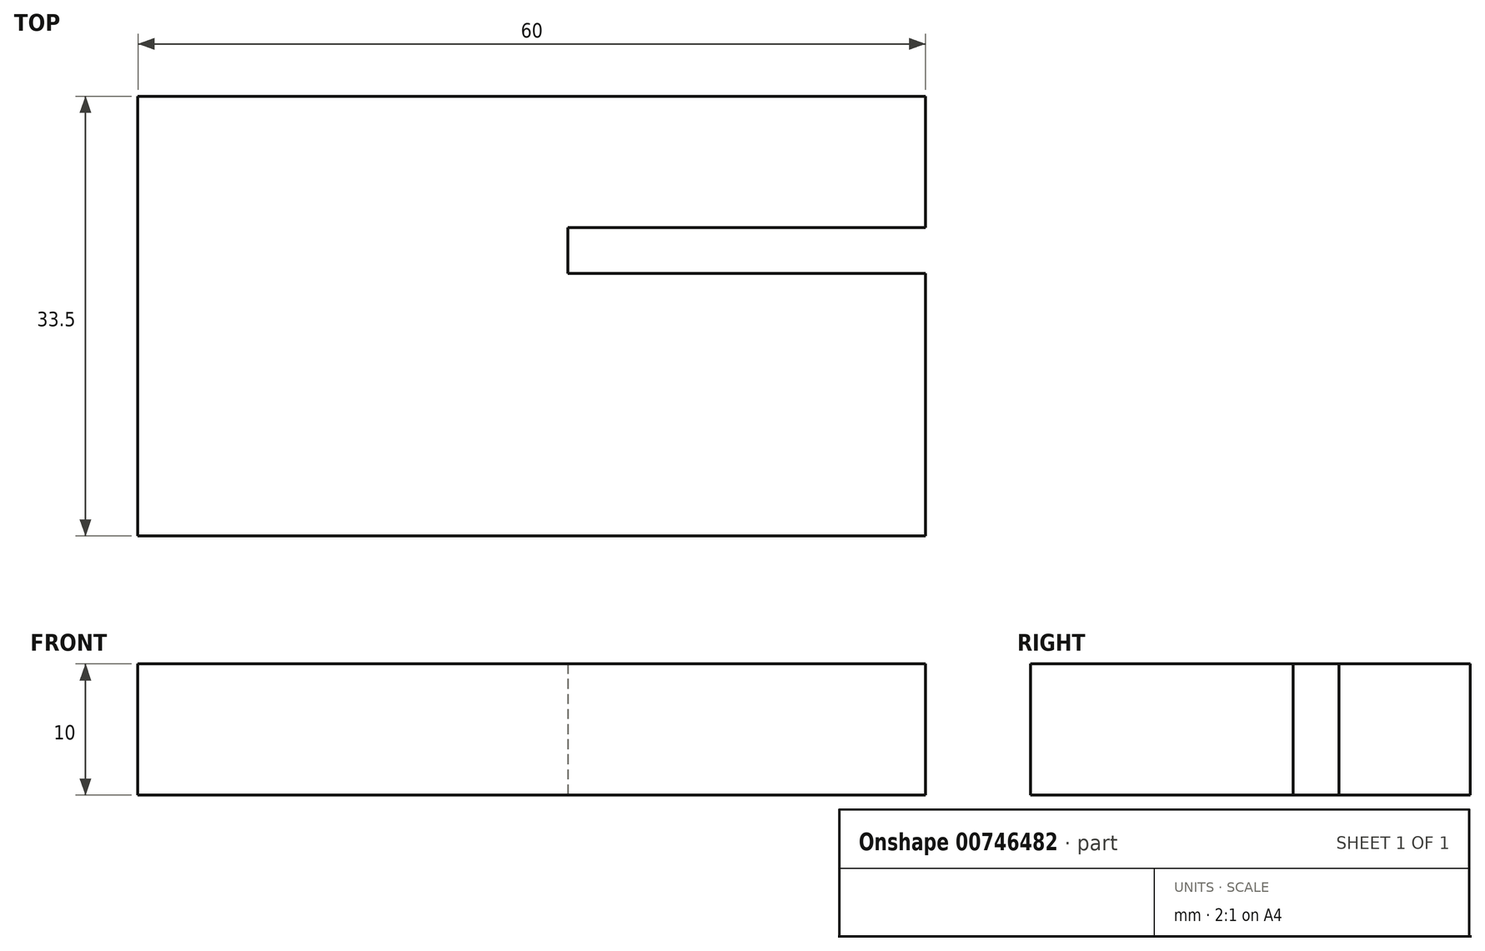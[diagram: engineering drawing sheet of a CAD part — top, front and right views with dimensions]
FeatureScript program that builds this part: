
annotation { "Feature Type Name" : "Feature", "Feature Type Description" : "" }
export const myFeature = defineFeature(function(context is Context, id is Id, definition is map)
    precondition{}
    {
        {
            var Q0;
            Q0=qCreatedBy(makeId("Top.planeOp"),FACE);
            var sketch = newSketch(context, id + "F0", { "sketchPlane" : qUnion([Q0])});
            skLineSegment(sketch, "E0", {"start": v(0, 0) * mm, "end": v(43.84, 0) * mm});
            skLineSegment(sketch, "E1", {"start": v(43.84, 0) * mm, "end": v(43.84, -10) * mm});
            skLineSegment(sketch, "E2", {"start": v(43.84, -10) * mm, "end": v(16.57, -10) * mm});
            skLineSegment(sketch, "E3", {"start": v(16.57, -10) * mm, "end": v(16.57, -13.5) * mm});
            skLineSegment(sketch, "E4", {"start": v(16.57, -13.5) * mm, "end": v(43.84, -13.5) * mm});
            skLineSegment(sketch, "E5", {"start": v(43.84, -13.5) * mm, "end": v(43.84, -33.5) * mm});
            skLineSegment(sketch, "E6", {"start": v(43.84, -33.5) * mm, "end": v(-16.16, -33.5) * mm});
            skLineSegment(sketch, "E7", {"start": v(-16.16, -33.5) * mm, "end": v(-16.16, 0) * mm});
            skLineSegment(sketch, "E8", {"start": v(-16.16, 0) * mm, "end": v(0, 0) * mm});
            skSolve(sketch);
        }
        {
            var Q0;
            Q0=makeQuery(id+"F0.imprint","IMPRINT",FACE,{"disambiguationData":[TD([[makeQuery(id+"F0.imprint","IMPRINT",EDGE,{"derivedFrom":sQuery(id+"F0.wireOp",EDGE,"E0")}),-1.0]])]});
            extrude(context, id + "F1", {"entities" : qUnion([Q0]), "depth" : 10 * mm, "offsetDistance" : 25 * mm});
        }
    });
